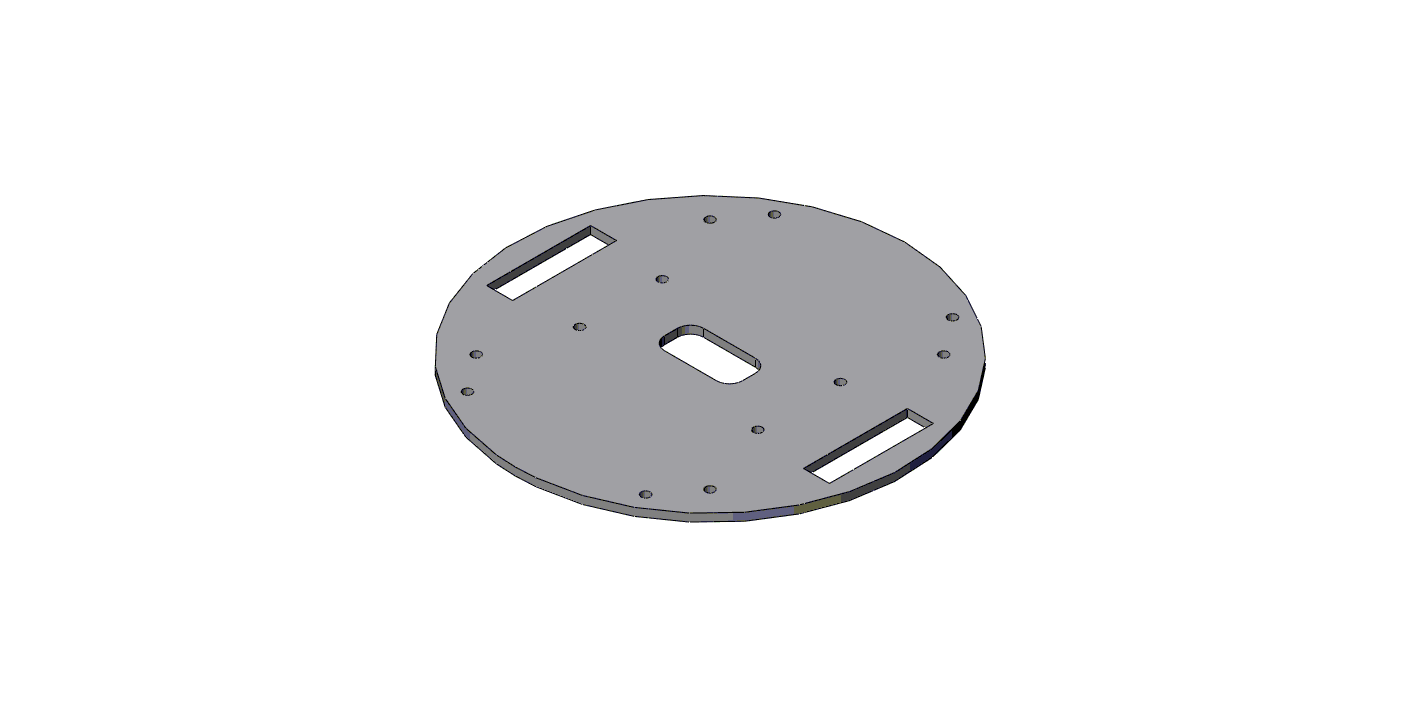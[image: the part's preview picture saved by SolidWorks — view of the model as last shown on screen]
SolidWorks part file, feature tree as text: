
SOLIDWORKS PART (.sldprt)
format: sldprt  version: not decoded by parser v0  size: 259,072 bytes
history: native  units: mm
features: sketch x5, cut_extrude x4, material x1, extrude x1, fillet x1 (+13 scaffold rows collapsed)
feature tree (25):
  scaffold x13  (default folders/planes/origin — collapsed)
  material  "Material <not specified>"
  sketch  "Sketch1"  dims[D1=150.0mm]
  extrude  "Boss-Extrude1"  Depth=3mm
  sketch  "Sketch2"  dims[D1=40.0mm D2=40.0mm D3=10.0mm D4=10.0mm D5=61.0mm D6=61.0mm]
  cut_extrude  "Cut-Extrude1"  Depth=6.35mm
  sketch  "Sketch8"  dims[D3=3.429mm D1=90.0mm D2=90.0mm]
  cut_extrude  "Cut-Extrude7"  [1 undecoded]
  sketch  "Sketch9"  dims[D1=30.0mm D2=15.0mm]
  cut_extrude  "Cut-Extrude8"  [1 undecoded]
  fillet  "Fillet1"  Radius=5mm
  sketch  "Sketch10"  dims[D7=3.429mm D1=68.58mm D2=43.18mm D3=68.58mm D4=43.18mm D5=37.5mm D6=37.5mm]
  cut_extrude  "Cut-Extrude9"  Depth=10mm
decode coverage: 9 of 11 modeling features carry decoded parameters
note: 2 parameter values undecoded
note: suppression state not decoded; provenance and decode notes live in map.json
